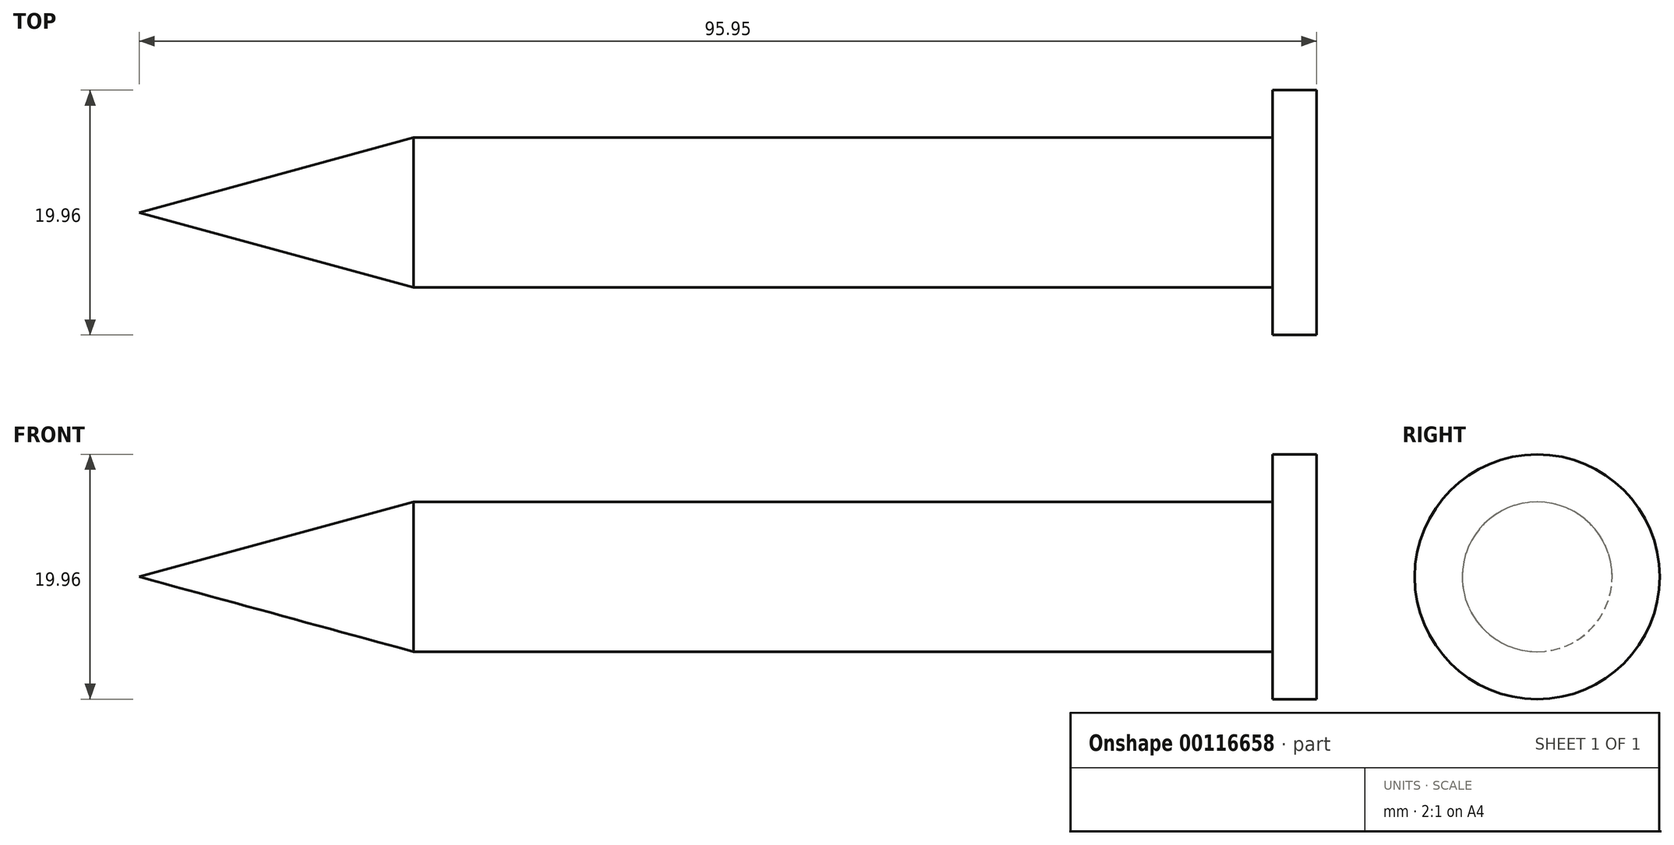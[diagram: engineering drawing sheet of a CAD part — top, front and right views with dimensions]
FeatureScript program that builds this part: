
annotation { "Feature Type Name" : "Feature", "Feature Type Description" : "" }
export const myFeature = defineFeature(function(context is Context, id is Id, definition is map)
    precondition{}
    {
        {
            var Q0;
            Q0=qCreatedBy(makeId("Front.planeOp"),FACE);
            var sketch = newSketch(context, id + "F0", { "sketchPlane" : qUnion([Q0])});
            skLineSegment(sketch, "E0.top", {"start": v(-25.33, 6.1) * mm, "end": v(44.7, 6.1) * mm});
            skLineSegment(sketch, "E0.left", {"start": v(-25.33, 0) * mm, "end": v(-25.33, 6.1) * mm});
            skLineSegment(sketch, "E0.right", {"start": v(44.7, 0) * mm, "end": v(44.7, 6.1) * mm});
            skLineSegment(sketch, "E1.bottom", {"start": v(44.7, 0) * mm, "end": v(48.27, 0) * mm});
            skLineSegment(sketch, "E1.top", {"start": v(44.7, 9.98) * mm, "end": v(48.27, 9.98) * mm});
            skLineSegment(sketch, "E1.left", {"start": v(44.7, 0) * mm, "end": v(44.7, 9.98) * mm});
            skLineSegment(sketch, "E1.right", {"start": v(48.27, 0) * mm, "end": v(48.27, 9.98) * mm});
            skLineSegment(sketch, "E2", {"start": v(-25.33, 6.1) * mm, "end": v(-47.68, 0) * mm});
            skLineSegment(sketch, "E3", {"start": v(-47.68, 0) * mm, "end": v(-25.33, 0) * mm});
            skLineSegment(sketch, "E4", {"start": v(-25.33, 0) * mm, "end": v(44.7, 0) * mm});
            skSolve(sketch);
        }
        {
            var Q0;
            Q0 = qSketchRegion(id + "F0", true);
            var Q1;
            Q1=sQuery(id+"F0.wireOp",EDGE,"E4");
            revolve(context, id + "F1", {"entities" : qUnion([Q0]), "axis" : qUnion([Q1]), "revolveType" : RevolveType.FULL});
        }
    });
